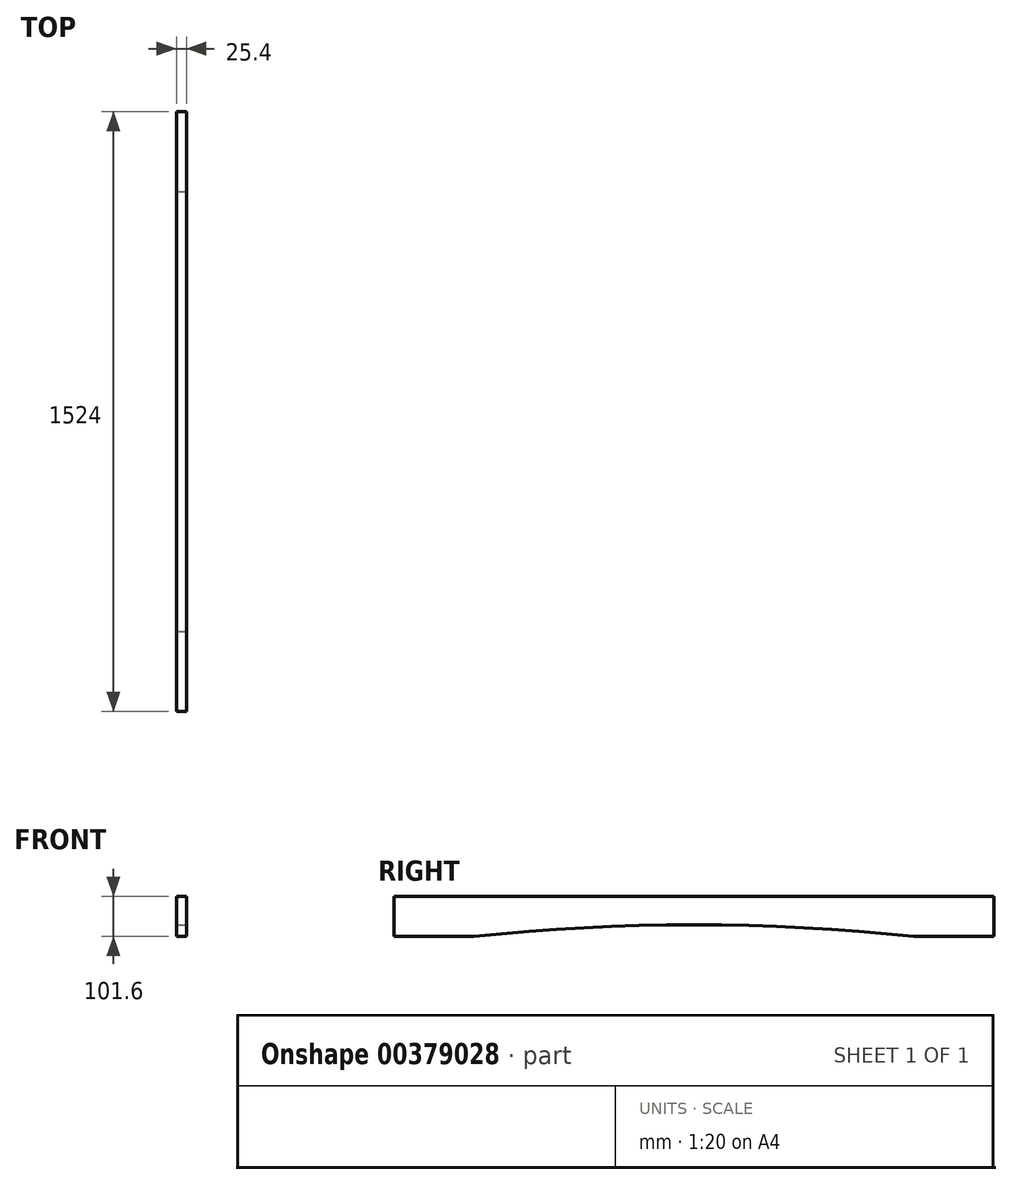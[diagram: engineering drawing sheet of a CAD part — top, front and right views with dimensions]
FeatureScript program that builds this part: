
annotation { "Feature Type Name" : "Feature", "Feature Type Description" : "" }
export const myFeature = defineFeature(function(context is Context, id is Id, definition is map)
    precondition{}
    {
        {
            var Q0;
            Q0=qCreatedBy(makeId("Right.planeOp"),FACE);
            var sketch = newSketch(context, id + "F0", { "sketchPlane" : qUnion([Q0])});
            skLineSegment(sketch, "E0", {"start": v(-762, 64.48) * mm, "end": v(762, 64.48) * mm});
            skLineSegment(sketch, "E1", {"start": v(-762, 64.48) * mm, "end": v(-762, -37.12) * mm});
            skLineSegment(sketch, "E2", {"start": v(762, 64.48) * mm, "end": v(762, -37.12) * mm});
            skLineSegment(sketch, "E3", {"start": v(-558.8, -37.12) * mm, "end": v(-762, -37.12) * mm});
            skLineSegment(sketch, "E4", {"start": v(762, -37.12) * mm, "end": v(558.8, -37.12) * mm});
            skArc(sketch, "E5", {"start": v(558.8, -37.12) * mm, "mid": v(0, -7.8) * mm, "end": v(-558.8, -37.12) * mm});
            skSolve(sketch);
        }
        {
            var Q0;
            Q0 = qSketchRegion(id + "F0", true);
            extrude(context, id + "F1", {"entities" : qUnion([Q0]), "oppositeDirection" : true, "depth" : 25.4 * mm});
        }
    });
